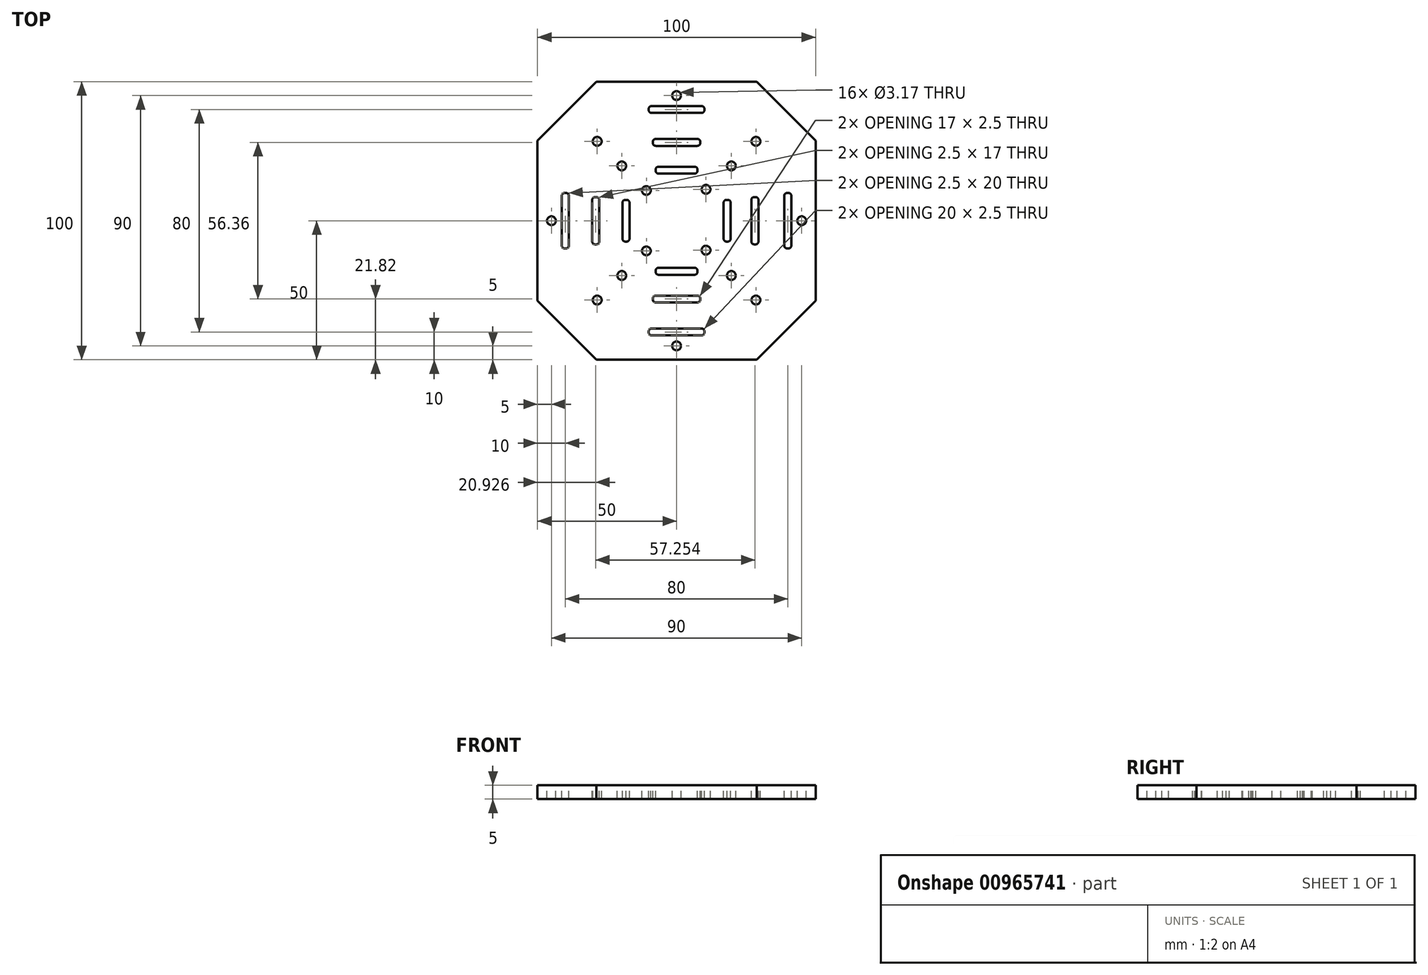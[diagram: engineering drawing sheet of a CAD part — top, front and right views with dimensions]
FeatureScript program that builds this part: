
annotation { "Feature Type Name" : "Feature", "Feature Type Description" : "" }
export const myFeature = defineFeature(function(context is Context, id is Id, definition is map)
    precondition{}
    {
        {
            var Q0;
            Q0=qCreatedBy(makeId("Top.planeOp"),FACE);
            var sketch = newSketch(context, id + "F0", { "sketchPlane" : qUnion([Q0])});
            skLineSegment(sketch, "E0.bottom", {"start": v(50, 50) * mm, "end": v(-50, 50) * mm});
            skLineSegment(sketch, "E0.top", {"start": v(50, -50) * mm, "end": v(-50, -50) * mm});
            skLineSegment(sketch, "E0.left", {"start": v(50, 50) * mm, "end": v(50, -50) * mm});
            skLineSegment(sketch, "E0.right", {"start": v(-50, 50) * mm, "end": v(-50, -50) * mm});
            skPoint(sketch, "E0.middle", {"position": v(0, 0) * mm});
            skSolve(sketch);
        }
        {
            var Q0;
            Q0 = qSketchRegion(id + "F0", true);
            extrude(context, id + "F1", {"entities" : qUnion([Q0]), "depth" : 5 * mm, "offsetDistance" : 25 * mm});
        }
        {
            var Q0;
            Q0=makeQuery(id+"F1.opExtrude","SWEPT_EDGE",EDGE,{"disambiguationData":[OSD([sQuery(id+"F0.wireOp",EDGE,"E0.top"),sQuery(id+"F0.wireOp",EDGE,"E0.left")])]});
            var Q1;
            Q1=makeQuery(id+"F1.opExtrude","SWEPT_EDGE",EDGE,{"disambiguationData":[OSD([sQuery(id+"F0.wireOp",EDGE,"E0.bottom"),sQuery(id+"F0.wireOp",EDGE,"E0.left")])]});
            var Q2;
            Q2=makeQuery(id+"F1.opExtrude","SWEPT_EDGE",EDGE,{"disambiguationData":[OSD([sQuery(id+"F0.wireOp",EDGE,"E0.top"),sQuery(id+"F0.wireOp",EDGE,"E0.right")])]});
            var Q3;
            Q3=makeQuery(id+"F1.opExtrude","SWEPT_EDGE",EDGE,{"disambiguationData":[OSD([sQuery(id+"F0.wireOp",EDGE,"E0.bottom"),sQuery(id+"F0.wireOp",EDGE,"E0.right")])]});
            chamfer(context, id + "F2", {"entities" : qUnion([Q0, Q1, Q2, Q3]), "chamferType" : ChamferType.OFFSET_ANGLE, "width" : 21.21 * mm, "oppositeDirection" : false, "angle" : 45 * degree, "tangentPropagation" : true});
        }
        {
            var Q0;
            Q0=makeQuery(id+"F1.opExtrude","CAP_FACE",FACE,{"disambiguationData":[OSD([sQuery(id+"F0.wireOp",EDGE,"E0.bottom"),sQuery(id+"F0.wireOp",EDGE,"E0.top"),sQuery(id+"F0.wireOp",EDGE,"E0.left"),sQuery(id+"F0.wireOp",EDGE,"E0.right")])],"isStart":false});
            var sketch = newSketch(context, id + "F3", { "sketchPlane" : qUnion([Q0])});
            skPoint(sketch, "E1.middle", {"position": v(0, 40) * mm});
            skLineSegment(sketch, "E2.bottom", {"start": v(41.25, -10) * mm, "end": v(38.75, -10) * mm});
            skLineSegment(sketch, "E2.top", {"start": v(41.25, 10) * mm, "end": v(38.75, 10) * mm});
            skLineSegment(sketch, "E2.left", {"start": v(41.25, -10) * mm, "end": v(41.25, 10) * mm});
            skLineSegment(sketch, "E2.right", {"start": v(38.75, -10) * mm, "end": v(38.75, 10) * mm});
            skPoint(sketch, "E2.middle", {"position": v(40, 0) * mm});
            skLineSegment(sketch, "E3.bottom", {"start": v(-38.75, 10) * mm, "end": v(-41.25, 10) * mm});
            skLineSegment(sketch, "E3.top", {"start": v(-38.75, -10) * mm, "end": v(-41.25, -10) * mm});
            skLineSegment(sketch, "E3.left", {"start": v(-38.75, 10) * mm, "end": v(-38.75, -10) * mm});
            skLineSegment(sketch, "E3.right", {"start": v(-41.25, 10) * mm, "end": v(-41.25, -10) * mm});
            skPoint(sketch, "E3.middle", {"position": v(-40, 0) * mm});
            skLineSegment(sketch, "E4.bottom", {"start": v(10, -41.25) * mm, "end": v(-10, -41.25) * mm});
            skLineSegment(sketch, "E4.top", {"start": v(10, -38.75) * mm, "end": v(-10, -38.75) * mm});
            skLineSegment(sketch, "E4.left", {"start": v(10, -41.25) * mm, "end": v(10, -38.75) * mm});
            skLineSegment(sketch, "E4.right", {"start": v(-10, -41.25) * mm, "end": v(-10, -38.75) * mm});
            skPoint(sketch, "E4.middle", {"position": v(0, -40) * mm});
            skLineSegment(sketch, "E5.bottom", {"start": v(10, 41.25) * mm, "end": v(-10, 41.25) * mm});
            skLineSegment(sketch, "E5.top", {"start": v(10, 38.75) * mm, "end": v(-10, 38.75) * mm});
            skLineSegment(sketch, "E5.left", {"start": v(10, 41.25) * mm, "end": v(10, 38.75) * mm});
            skLineSegment(sketch, "E5.right", {"start": v(-10, 41.25) * mm, "end": v(-10, 38.75) * mm});
            skCircle(sketch, "E6", {"center": v(-45, 0) * mm, "radius": 1.59 * mm});
            skCircle(sketch, "E7", {"center": v(0, 45) * mm, "radius": 1.59 * mm});
            skCircle(sketch, "E8", {"center": v(0, -45) * mm, "radius": 1.59 * mm});
            skCircle(sketch, "E9", {"center": v(45, 0) * mm, "radius": 1.59 * mm});
            skCircle(sketch, "E10", {"center": v(-28.54, 28.54) * mm, "radius": 1.59 * mm});
            skCircle(sketch, "E11", {"center": v(-19.7, 19.7) * mm, "radius": 1.59 * mm});
            skCircle(sketch, "E12", {"center": v(-10.86, 10.86) * mm, "radius": 1.59 * mm});
            skCircle(sketch, "E13", {"center": v(10.6, 11.28) * mm, "radius": 1.59 * mm});
            skCircle(sketch, "E14", {"center": v(19.7, 19.7) * mm, "radius": 1.59 * mm});
            skCircle(sketch, "E15", {"center": v(28.54, 28.54) * mm, "radius": 1.59 * mm});
            skCircle(sketch, "E16", {"center": v(10.6, -10.6) * mm, "radius": 1.59 * mm});
            skCircle(sketch, "E17", {"center": v(19.7, -19.7) * mm, "radius": 1.59 * mm});
            skCircle(sketch, "E18", {"center": v(28.54, -28.54) * mm, "radius": 1.59 * mm});
            skCircle(sketch, "E19", {"center": v(-28.54, -28.54) * mm, "radius": 1.59 * mm});
            skCircle(sketch, "E20", {"center": v(-19.7, -19.7) * mm, "radius": 1.59 * mm});
            skCircle(sketch, "E21", {"center": v(-10.86, -10.86) * mm, "radius": 1.59 * mm});
            skSolve(sketch);
        }
        {
            var Q0;
            Q0=makeQuery(id+"F3.imprint","IMPRINT",FACE,{"disambiguationData":[TD([[makeQuery(id+"F3.imprint","IMPRINT",EDGE,{"derivedFrom":sQuery(id+"F3.wireOp",EDGE,"E2.bottom")}),-1.0]])]});
            var Q1;
            Q1=makeQuery(id+"F3.imprint","IMPRINT",FACE,{"disambiguationData":[TD([[makeQuery(id+"F3.imprint","IMPRINT",EDGE,{"derivedFrom":sQuery(id+"F3.wireOp",EDGE,"E9")}),1.0]])]});
            var Q2;
            Q2=makeQuery(id+"F3.imprint","IMPRINT",FACE,{"disambiguationData":[TD([[makeQuery(id+"F3.imprint","IMPRINT",EDGE,{"derivedFrom":sQuery(id+"F3.wireOp",EDGE,"E7")}),1.0]])]});
            var Q3;
            Q3=makeQuery(id+"F3.imprint","IMPRINT",FACE,{"disambiguationData":[TD([[makeQuery(id+"F3.imprint","IMPRINT",EDGE,{"derivedFrom":sQuery(id+"F3.wireOp",EDGE,"E5.bottom")}),1.0]])]});
            var Q4;
            Q4=makeQuery(id+"F3.imprint","IMPRINT",FACE,{"disambiguationData":[TD([[makeQuery(id+"F3.imprint","IMPRINT",EDGE,{"derivedFrom":sQuery(id+"F3.wireOp",EDGE,"E14")}),1.0]])]});
            var Q5;
            Q5=makeQuery(id+"F3.imprint","IMPRINT",FACE,{"disambiguationData":[TD([[makeQuery(id+"F3.imprint","IMPRINT",EDGE,{"derivedFrom":sQuery(id+"F3.wireOp",EDGE,"E10")}),1.0]])]});
            var Q6;
            Q6=makeQuery(id+"F3.imprint","IMPRINT",FACE,{"disambiguationData":[TD([[makeQuery(id+"F3.imprint","IMPRINT",EDGE,{"derivedFrom":sQuery(id+"F3.wireOp",EDGE,"E15")}),1.0]])]});
            var Q7;
            Q7=makeQuery(id+"F3.imprint","IMPRINT",FACE,{"disambiguationData":[TD([[makeQuery(id+"F3.imprint","IMPRINT",EDGE,{"derivedFrom":sQuery(id+"F3.wireOp",EDGE,"E13")}),1.0]])]});
            var Q8;
            Q8=makeQuery(id+"F3.imprint","IMPRINT",FACE,{"disambiguationData":[TD([[makeQuery(id+"F3.imprint","IMPRINT",EDGE,{"derivedFrom":sQuery(id+"F3.wireOp",EDGE,"E11")}),1.0]])]});
            var Q9;
            Q9=makeQuery(id+"F3.imprint","IMPRINT",FACE,{"disambiguationData":[TD([[makeQuery(id+"F3.imprint","IMPRINT",EDGE,{"derivedFrom":sQuery(id+"F3.wireOp",EDGE,"E6")}),1.0]])]});
            var Q10;
            Q10=makeQuery(id+"F3.imprint","IMPRINT",FACE,{"disambiguationData":[TD([[makeQuery(id+"F3.imprint","IMPRINT",EDGE,{"derivedFrom":sQuery(id+"F3.wireOp",EDGE,"E3.bottom")}),1.0]])]});
            var Q11;
            Q11=makeQuery(id+"F3.imprint","IMPRINT",FACE,{"disambiguationData":[TD([[makeQuery(id+"F3.imprint","IMPRINT",EDGE,{"derivedFrom":sQuery(id+"F3.wireOp",EDGE,"E12")}),1.0]])]});
            var Q12;
            Q12=makeQuery(id+"F3.imprint","IMPRINT",FACE,{"disambiguationData":[TD([[makeQuery(id+"F3.imprint","IMPRINT",EDGE,{"derivedFrom":sQuery(id+"F3.wireOp",EDGE,"E8")}),1.0]])]});
            var Q13;
            Q13=makeQuery(id+"F3.imprint","IMPRINT",FACE,{"disambiguationData":[TD([[makeQuery(id+"F3.imprint","IMPRINT",EDGE,{"derivedFrom":sQuery(id+"F3.wireOp",EDGE,"E4.bottom")}),-1.0]])]});
            var Q14;
            Q14=makeQuery(id+"F3.imprint","IMPRINT",FACE,{"disambiguationData":[TD([[makeQuery(id+"F3.imprint","IMPRINT",EDGE,{"derivedFrom":sQuery(id+"F3.wireOp",EDGE,"E16")}),1.0]])]});
            var Q15;
            Q15=makeQuery(id+"F3.imprint","IMPRINT",FACE,{"disambiguationData":[TD([[makeQuery(id+"F3.imprint","IMPRINT",EDGE,{"derivedFrom":sQuery(id+"F3.wireOp",EDGE,"E17")}),1.0]])]});
            var Q16;
            Q16=makeQuery(id+"F3.imprint","IMPRINT",FACE,{"disambiguationData":[TD([[makeQuery(id+"F3.imprint","IMPRINT",EDGE,{"derivedFrom":sQuery(id+"F3.wireOp",EDGE,"E18")}),1.0]])]});
            var Q17;
            Q17=makeQuery(id+"F3.imprint","IMPRINT",FACE,{"disambiguationData":[TD([[makeQuery(id+"F3.imprint","IMPRINT",EDGE,{"derivedFrom":sQuery(id+"F3.wireOp",EDGE,"E19")}),1.0]])]});
            var Q18;
            Q18=makeQuery(id+"F3.imprint","IMPRINT",FACE,{"disambiguationData":[TD([[makeQuery(id+"F3.imprint","IMPRINT",EDGE,{"derivedFrom":sQuery(id+"F3.wireOp",EDGE,"E20")}),1.0]])]});
            var Q19;
            Q19=makeQuery(id+"F3.imprint","IMPRINT",FACE,{"disambiguationData":[TD([[makeQuery(id+"F3.imprint","IMPRINT",EDGE,{"derivedFrom":sQuery(id+"F3.wireOp",EDGE,"E21")}),1.0]])]});
            extrude(context, id + "F4", {"entities" : qUnion([Q0, Q1, Q2, Q3, Q4, Q5, Q6, Q7, Q8, Q9, Q10, Q11, Q12, Q13, Q14, Q15, Q16, Q17, Q18, Q19]), "operationType" : NewBodyOperationType.REMOVE, "oppositeDirection" : true, "depth" : 5 * mm, "offsetDistance" : 25 * mm});
        }
        {
            var Q0;
            Q0=makeQuery(id+"F4.boolean.opBoolean","COPY",EDGE,{"derivedFrom":makeQuery(id+"F4.opExtrude","SWEPT_EDGE",EDGE,{"disambiguationData":[OSD([sQuery(id+"F3.wireOp",EDGE,"E3.bottom"),sQuery(id+"F3.wireOp",EDGE,"E3.right")])]})});
            var Q1;
            Q1=makeQuery(id+"F4.boolean.opBoolean","COPY",EDGE,{"derivedFrom":makeQuery(id+"F4.opExtrude","SWEPT_EDGE",EDGE,{"disambiguationData":[OSD([sQuery(id+"F3.wireOp",EDGE,"E4.top"),sQuery(id+"F3.wireOp",EDGE,"E4.right")])]})});
            var Q2;
            Q2=makeQuery(id+"F4.boolean.opBoolean","COPY",EDGE,{"derivedFrom":makeQuery(id+"F4.opExtrude","SWEPT_EDGE",EDGE,{"disambiguationData":[OSD([sQuery(id+"F3.wireOp",EDGE,"E2.top"),sQuery(id+"F3.wireOp",EDGE,"E2.right")])]})});
            var Q3;
            Q3=makeQuery(id+"F4.boolean.opBoolean","COPY",EDGE,{"derivedFrom":makeQuery(id+"F4.opExtrude","SWEPT_EDGE",EDGE,{"disambiguationData":[OSD([sQuery(id+"F3.wireOp",EDGE,"E5.bottom"),sQuery(id+"F3.wireOp",EDGE,"E5.right")])]})});
            var Q4;
            Q4=makeQuery(id+"F4.boolean.opBoolean","COPY",EDGE,{"derivedFrom":makeQuery(id+"F4.opExtrude","SWEPT_EDGE",EDGE,{"disambiguationData":[OSD([sQuery(id+"F3.wireOp",EDGE,"E4.top"),sQuery(id+"F3.wireOp",EDGE,"E4.left")])]})});
            var Q5;
            Q5=makeQuery(id+"F4.boolean.opBoolean","COPY",EDGE,{"derivedFrom":makeQuery(id+"F4.opExtrude","SWEPT_EDGE",EDGE,{"disambiguationData":[OSD([sQuery(id+"F3.wireOp",EDGE,"E2.top"),sQuery(id+"F3.wireOp",EDGE,"E2.left")])]})});
            var Q6;
            Q6=makeQuery(id+"F4.boolean.opBoolean","COPY",EDGE,{"derivedFrom":makeQuery(id+"F4.opExtrude","SWEPT_EDGE",EDGE,{"disambiguationData":[OSD([sQuery(id+"F3.wireOp",EDGE,"E3.bottom"),sQuery(id+"F3.wireOp",EDGE,"E3.left")])]})});
            var Q7;
            Q7=makeQuery(id+"F4.boolean.opBoolean","COPY",EDGE,{"derivedFrom":makeQuery(id+"F4.opExtrude","SWEPT_EDGE",EDGE,{"disambiguationData":[OSD([sQuery(id+"F3.wireOp",EDGE,"E5.bottom"),sQuery(id+"F3.wireOp",EDGE,"E5.left")])]})});
            var Q8;
            Q8=makeQuery(id+"F4.boolean.opBoolean","COPY",EDGE,{"derivedFrom":makeQuery(id+"F4.opExtrude","SWEPT_EDGE",EDGE,{"disambiguationData":[OSD([sQuery(id+"F3.wireOp",EDGE,"E2.bottom"),sQuery(id+"F3.wireOp",EDGE,"E2.left")])]})});
            var Q9;
            Q9=makeQuery(id+"F4.boolean.opBoolean","COPY",EDGE,{"derivedFrom":makeQuery(id+"F4.opExtrude","SWEPT_EDGE",EDGE,{"disambiguationData":[OSD([sQuery(id+"F3.wireOp",EDGE,"E4.bottom"),sQuery(id+"F3.wireOp",EDGE,"E4.left")])]})});
            var Q10;
            Q10=makeQuery(id+"F4.boolean.opBoolean","COPY",EDGE,{"derivedFrom":makeQuery(id+"F4.opExtrude","SWEPT_EDGE",EDGE,{"disambiguationData":[OSD([sQuery(id+"F3.wireOp",EDGE,"E5.top"),sQuery(id+"F3.wireOp",EDGE,"E5.left")])]})});
            var Q11;
            Q11=makeQuery(id+"F4.boolean.opBoolean","COPY",EDGE,{"derivedFrom":makeQuery(id+"F4.opExtrude","SWEPT_EDGE",EDGE,{"disambiguationData":[OSD([sQuery(id+"F3.wireOp",EDGE,"E3.top"),sQuery(id+"F3.wireOp",EDGE,"E3.left")])]})});
            var Q12;
            Q12=makeQuery(id+"F4.boolean.opBoolean","COPY",EDGE,{"derivedFrom":makeQuery(id+"F4.opExtrude","SWEPT_EDGE",EDGE,{"disambiguationData":[OSD([sQuery(id+"F3.wireOp",EDGE,"E5.top"),sQuery(id+"F3.wireOp",EDGE,"E5.right")])]})});
            var Q13;
            Q13=makeQuery(id+"F4.boolean.opBoolean","COPY",EDGE,{"derivedFrom":makeQuery(id+"F4.opExtrude","SWEPT_EDGE",EDGE,{"disambiguationData":[OSD([sQuery(id+"F3.wireOp",EDGE,"E2.bottom"),sQuery(id+"F3.wireOp",EDGE,"E2.right")])]})});
            var Q14;
            Q14=makeQuery(id+"F4.boolean.opBoolean","COPY",EDGE,{"derivedFrom":makeQuery(id+"F4.opExtrude","SWEPT_EDGE",EDGE,{"disambiguationData":[OSD([sQuery(id+"F3.wireOp",EDGE,"E3.top"),sQuery(id+"F3.wireOp",EDGE,"E3.right")])]})});
            var Q15;
            Q15=makeQuery(id+"F4.boolean.opBoolean","COPY",EDGE,{"derivedFrom":makeQuery(id+"F4.opExtrude","SWEPT_EDGE",EDGE,{"disambiguationData":[OSD([sQuery(id+"F3.wireOp",EDGE,"E4.bottom"),sQuery(id+"F3.wireOp",EDGE,"E4.right")])]})});
            fillet(context, id + "F5", {"entities" : qUnion([Q0, Q1, Q2, Q3, Q4, Q5, Q6, Q7, Q8, Q9, Q10, Q11, Q12, Q13, Q14, Q15]), "radius" : 1 * mm, "tangentPropagation" : true, "allowEdgeOverflow" : false});
        }
        {
            var Q0;
            Q0=makeQuery(id+"F1.opExtrude","CAP_FACE",FACE,{"disambiguationData":[OSD([sQuery(id+"F0.wireOp",EDGE,"E0.bottom"),sQuery(id+"F0.wireOp",EDGE,"E0.top"),sQuery(id+"F0.wireOp",EDGE,"E0.left"),sQuery(id+"F0.wireOp",EDGE,"E0.right")])],"isStart":false});
            var sketch = newSketch(context, id + "F6", { "sketchPlane" : qUnion([Q0])});
            skLineSegment(sketch, "E22", {"start": v(-18.18, 18.18) * mm, "end": v(-7.5, 18.18) * mm});
            skLineSegment(sketch, "E23.bottom", {"start": v(7.5, 19.43) * mm, "end": v(-7.5, 19.43) * mm});
            skLineSegment(sketch, "E23.top", {"start": v(7.5, 16.93) * mm, "end": v(-7.5, 16.93) * mm});
            skLineSegment(sketch, "E23.left", {"start": v(7.5, 19.43) * mm, "end": v(7.5, 16.93) * mm});
            skLineSegment(sketch, "E23.right", {"start": v(-7.5, 19.43) * mm, "end": v(-7.5, 16.93) * mm});
            skPoint(sketch, "E23.middle", {"position": v(0, 18.18) * mm});
            skLineSegment(sketch, "E24.bottom", {"start": v(-19.43, 7.5) * mm, "end": v(-16.93, 7.5) * mm});
            skLineSegment(sketch, "E24.top", {"start": v(-19.43, -7.5) * mm, "end": v(-16.93, -7.5) * mm});
            skLineSegment(sketch, "E24.left", {"start": v(-19.43, 7.5) * mm, "end": v(-19.43, -7.5) * mm});
            skLineSegment(sketch, "E24.right", {"start": v(-16.93, 7.5) * mm, "end": v(-16.93, -7.5) * mm});
            skPoint(sketch, "E24.middle", {"position": v(-18.18, 0) * mm});
            skLineSegment(sketch, "E25.bottom", {"start": v(7.5, -16.93) * mm, "end": v(-7.5, -16.93) * mm});
            skLineSegment(sketch, "E25.top", {"start": v(7.5, -19.43) * mm, "end": v(-7.5, -19.43) * mm});
            skLineSegment(sketch, "E25.left", {"start": v(7.5, -16.93) * mm, "end": v(7.5, -19.43) * mm});
            skLineSegment(sketch, "E25.right", {"start": v(-7.5, -16.93) * mm, "end": v(-7.5, -19.43) * mm});
            skPoint(sketch, "E25.middle", {"position": v(0, -18.18) * mm});
            skLineSegment(sketch, "E26.bottom", {"start": v(19.43, 7.5) * mm, "end": v(16.93, 7.5) * mm});
            skLineSegment(sketch, "E26.top", {"start": v(19.43, -7.5) * mm, "end": v(16.93, -7.5) * mm});
            skLineSegment(sketch, "E26.left", {"start": v(19.43, 7.5) * mm, "end": v(19.43, -7.5) * mm});
            skLineSegment(sketch, "E26.right", {"start": v(16.93, 7.5) * mm, "end": v(16.93, -7.5) * mm});
            skPoint(sketch, "E26.middle", {"position": v(18.18, 0) * mm});
            skLineSegment(sketch, "E27.bottom", {"start": v(-27.82, 8.5) * mm, "end": v(-30.32, 8.5) * mm});
            skLineSegment(sketch, "E27.top", {"start": v(-27.82, -8.5) * mm, "end": v(-30.32, -8.5) * mm});
            skLineSegment(sketch, "E27.left", {"start": v(-27.82, 8.5) * mm, "end": v(-27.82, -8.5) * mm});
            skLineSegment(sketch, "E27.right", {"start": v(-30.32, 8.5) * mm, "end": v(-30.32, -8.5) * mm});
            skPoint(sketch, "E27.middle", {"position": v(-29.07, 0) * mm});
            skLineSegment(sketch, "E28", {"start": v(0, 18.18) * mm, "end": v(0, 19.43) * mm});
            skLineSegment(sketch, "E29", {"start": v(0, -18.18) * mm, "end": v(0, -19.43) * mm});
            skLineSegment(sketch, "E30.bottom", {"start": v(8.5, -26.93) * mm, "end": v(-8.5, -26.93) * mm});
            skLineSegment(sketch, "E30.top", {"start": v(8.5, -29.43) * mm, "end": v(-8.5, -29.43) * mm});
            skLineSegment(sketch, "E30.left", {"start": v(8.5, -26.93) * mm, "end": v(8.5, -29.43) * mm});
            skLineSegment(sketch, "E30.right", {"start": v(-8.5, -26.93) * mm, "end": v(-8.5, -29.43) * mm});
            skPoint(sketch, "E30.middle", {"position": v(0, -28.18) * mm});
            skLineSegment(sketch, "E31.bottom", {"start": v(29.43, 8.5) * mm, "end": v(26.93, 8.5) * mm});
            skLineSegment(sketch, "E31.top", {"start": v(29.43, -8.5) * mm, "end": v(26.93, -8.5) * mm});
            skLineSegment(sketch, "E31.left", {"start": v(29.43, 8.5) * mm, "end": v(29.43, -8.5) * mm});
            skLineSegment(sketch, "E31.right", {"start": v(26.93, 8.5) * mm, "end": v(26.93, -8.5) * mm});
            skPoint(sketch, "E31.middle", {"position": v(28.18, 0) * mm});
            skLineSegment(sketch, "E32.bottom", {"start": v(8.5, 29.43) * mm, "end": v(-8.5, 29.43) * mm});
            skLineSegment(sketch, "E32.top", {"start": v(8.5, 26.93) * mm, "end": v(-8.5, 26.93) * mm});
            skLineSegment(sketch, "E32.left", {"start": v(8.5, 29.43) * mm, "end": v(8.5, 26.93) * mm});
            skLineSegment(sketch, "E32.right", {"start": v(-8.5, 29.43) * mm, "end": v(-8.5, 26.93) * mm});
            skPoint(sketch, "E32.middle", {"position": v(0, 28.18) * mm});
            skLineSegment(sketch, "E33.trimOffspring", {"start": v(-27.82, 0) * mm, "end": v(-29.07, 0) * mm});
            skPoint(sketch, "E34.orphan", {"position": v(-18.18, -18.18) * mm});
            skLineSegment(sketch, "E35.trimOffspring", {"start": v(0, -26.93) * mm, "end": v(0, -28.18) * mm});
            skLineSegment(sketch, "E36.trimOffspring", {"start": v(0, 26.93) * mm, "end": v(0, 28.18) * mm});
            skPoint(sketch, "E37.orphan", {"position": v(18.18, 18.18) * mm});
            skLineSegment(sketch, "E38.trimOffspring", {"start": v(26.93, 0) * mm, "end": v(28.18, 0) * mm});
            skPoint(sketch, "E39.end.orphan", {"position": v(18.18, -18.18) * mm});
            skSolve(sketch);
        }
        {
            var Q0;
            Q0 = qSketchRegion(id + "F6", true);
            extrude(context, id + "F7", {"entities" : qUnion([Q0]), "operationType" : NewBodyOperationType.REMOVE, "oppositeDirection" : true, "depth" : 5 * mm, "offsetDistance" : 25 * mm});
        }
        {
            var Q0;
            Q0=makeQuery(id+"F7.boolean.opBoolean","COPY",EDGE,{"derivedFrom":makeQuery(id+"F7.opExtrude","SWEPT_EDGE",EDGE,{"disambiguationData":[OSD([sQuery(id+"F6.wireOp",EDGE,"E27.bottom"),sQuery(id+"F6.wireOp",EDGE,"E27.right")])]})});
            var Q1;
            Q1=makeQuery(id+"F7.boolean.opBoolean","COPY",EDGE,{"derivedFrom":makeQuery(id+"F7.opExtrude","SWEPT_EDGE",EDGE,{"disambiguationData":[OSD([sQuery(id+"F6.wireOp",EDGE,"E24.bottom"),sQuery(id+"F6.wireOp",EDGE,"E24.left")])]})});
            var Q2;
            Q2=makeQuery(id+"F7.boolean.opBoolean","COPY",EDGE,{"derivedFrom":makeQuery(id+"F7.opExtrude","SWEPT_EDGE",EDGE,{"disambiguationData":[OSD([sQuery(id+"F6.wireOp",EDGE,"E32.bottom"),sQuery(id+"F6.wireOp",EDGE,"E32.right")])]})});
            var Q3;
            Q3=makeQuery(id+"F7.boolean.opBoolean","COPY",EDGE,{"derivedFrom":makeQuery(id+"F7.opExtrude","SWEPT_EDGE",EDGE,{"disambiguationData":[OSD([sQuery(id+"F6.wireOp",EDGE,"E23.bottom"),sQuery(id+"F6.wireOp",EDGE,"E23.right")])]})});
            var Q4;
            Q4=makeQuery(id+"F7.boolean.opBoolean","COPY",EDGE,{"derivedFrom":makeQuery(id+"F7.opExtrude","SWEPT_EDGE",EDGE,{"disambiguationData":[OSD([sQuery(id+"F6.wireOp",EDGE,"E25.bottom"),sQuery(id+"F6.wireOp",EDGE,"E25.right")])]})});
            var Q5;
            Q5=makeQuery(id+"F7.boolean.opBoolean","COPY",EDGE,{"derivedFrom":makeQuery(id+"F7.opExtrude","SWEPT_EDGE",EDGE,{"disambiguationData":[OSD([sQuery(id+"F6.wireOp",EDGE,"E30.bottom"),sQuery(id+"F6.wireOp",EDGE,"E30.right")])]})});
            var Q6;
            Q6=makeQuery(id+"F7.boolean.opBoolean","COPY",EDGE,{"derivedFrom":makeQuery(id+"F7.opExtrude","SWEPT_EDGE",EDGE,{"disambiguationData":[OSD([sQuery(id+"F6.wireOp",EDGE,"E26.bottom"),sQuery(id+"F6.wireOp",EDGE,"E26.right")])]})});
            var Q7;
            Q7=makeQuery(id+"F7.boolean.opBoolean","COPY",EDGE,{"derivedFrom":makeQuery(id+"F7.opExtrude","SWEPT_EDGE",EDGE,{"disambiguationData":[OSD([sQuery(id+"F6.wireOp",EDGE,"E31.bottom"),sQuery(id+"F6.wireOp",EDGE,"E31.right")])]})});
            var Q8;
            Q8=makeQuery(id+"F7.boolean.opBoolean","COPY",EDGE,{"derivedFrom":makeQuery(id+"F7.opExtrude","SWEPT_EDGE",EDGE,{"disambiguationData":[OSD([sQuery(id+"F6.wireOp",EDGE,"E32.bottom"),sQuery(id+"F6.wireOp",EDGE,"E32.left")])]})});
            var Q9;
            Q9=makeQuery(id+"F7.boolean.opBoolean","COPY",EDGE,{"derivedFrom":makeQuery(id+"F7.opExtrude","SWEPT_EDGE",EDGE,{"disambiguationData":[OSD([sQuery(id+"F6.wireOp",EDGE,"E23.bottom"),sQuery(id+"F6.wireOp",EDGE,"E23.left")])]})});
            var Q10;
            Q10=makeQuery(id+"F7.boolean.opBoolean","COPY",EDGE,{"derivedFrom":makeQuery(id+"F7.opExtrude","SWEPT_EDGE",EDGE,{"disambiguationData":[OSD([sQuery(id+"F6.wireOp",EDGE,"E27.bottom"),sQuery(id+"F6.wireOp",EDGE,"E27.left")])]})});
            var Q11;
            Q11=makeQuery(id+"F7.boolean.opBoolean","COPY",EDGE,{"derivedFrom":makeQuery(id+"F7.opExtrude","SWEPT_EDGE",EDGE,{"disambiguationData":[OSD([sQuery(id+"F6.wireOp",EDGE,"E24.bottom"),sQuery(id+"F6.wireOp",EDGE,"E24.right")])]})});
            var Q12;
            Q12=makeQuery(id+"F7.boolean.opBoolean","COPY",EDGE,{"derivedFrom":makeQuery(id+"F7.opExtrude","SWEPT_EDGE",EDGE,{"disambiguationData":[OSD([sQuery(id+"F6.wireOp",EDGE,"E31.bottom"),sQuery(id+"F6.wireOp",EDGE,"E31.left")])]})});
            var Q13;
            Q13=makeQuery(id+"F7.boolean.opBoolean","COPY",EDGE,{"derivedFrom":makeQuery(id+"F7.opExtrude","SWEPT_EDGE",EDGE,{"disambiguationData":[OSD([sQuery(id+"F6.wireOp",EDGE,"E26.bottom"),sQuery(id+"F6.wireOp",EDGE,"E26.left")])]})});
            var Q14;
            Q14=makeQuery(id+"F7.boolean.opBoolean","COPY",EDGE,{"derivedFrom":makeQuery(id+"F7.opExtrude","SWEPT_EDGE",EDGE,{"disambiguationData":[OSD([sQuery(id+"F6.wireOp",EDGE,"E25.bottom"),sQuery(id+"F6.wireOp",EDGE,"E25.left")])]})});
            var Q15;
            Q15=makeQuery(id+"F7.boolean.opBoolean","COPY",EDGE,{"derivedFrom":makeQuery(id+"F7.opExtrude","SWEPT_EDGE",EDGE,{"disambiguationData":[OSD([sQuery(id+"F6.wireOp",EDGE,"E30.bottom"),sQuery(id+"F6.wireOp",EDGE,"E30.left")])]})});
            var Q16;
            Q16=makeQuery(id+"F7.boolean.opBoolean","COPY",EDGE,{"derivedFrom":makeQuery(id+"F7.opExtrude","SWEPT_EDGE",EDGE,{"disambiguationData":[OSD([sQuery(id+"F6.wireOp",EDGE,"E31.top"),sQuery(id+"F6.wireOp",EDGE,"E31.left")])]})});
            var Q17;
            Q17=makeQuery(id+"F7.boolean.opBoolean","COPY",EDGE,{"derivedFrom":makeQuery(id+"F7.opExtrude","SWEPT_EDGE",EDGE,{"disambiguationData":[OSD([sQuery(id+"F6.wireOp",EDGE,"E26.top"),sQuery(id+"F6.wireOp",EDGE,"E26.left")])]})});
            var Q18;
            Q18=makeQuery(id+"F7.boolean.opBoolean","COPY",EDGE,{"derivedFrom":makeQuery(id+"F7.opExtrude","SWEPT_EDGE",EDGE,{"disambiguationData":[OSD([sQuery(id+"F6.wireOp",EDGE,"E25.top"),sQuery(id+"F6.wireOp",EDGE,"E25.left")])]})});
            var Q19;
            Q19=makeQuery(id+"F7.boolean.opBoolean","COPY",EDGE,{"derivedFrom":makeQuery(id+"F7.opExtrude","SWEPT_EDGE",EDGE,{"disambiguationData":[OSD([sQuery(id+"F6.wireOp",EDGE,"E30.top"),sQuery(id+"F6.wireOp",EDGE,"E30.left")])]})});
            var Q20;
            Q20=makeQuery(id+"F7.boolean.opBoolean","COPY",EDGE,{"derivedFrom":makeQuery(id+"F7.opExtrude","SWEPT_EDGE",EDGE,{"disambiguationData":[OSD([sQuery(id+"F6.wireOp",EDGE,"E23.top"),sQuery(id+"F6.wireOp",EDGE,"E23.left")])]})});
            var Q21;
            Q21=makeQuery(id+"F7.boolean.opBoolean","COPY",EDGE,{"derivedFrom":makeQuery(id+"F7.opExtrude","SWEPT_EDGE",EDGE,{"disambiguationData":[OSD([sQuery(id+"F6.wireOp",EDGE,"E32.top"),sQuery(id+"F6.wireOp",EDGE,"E32.left")])]})});
            var Q22;
            Q22=makeQuery(id+"F7.boolean.opBoolean","COPY",EDGE,{"derivedFrom":makeQuery(id+"F7.opExtrude","SWEPT_EDGE",EDGE,{"disambiguationData":[OSD([sQuery(id+"F6.wireOp",EDGE,"E27.top"),sQuery(id+"F6.wireOp",EDGE,"E27.left")])]})});
            var Q23;
            Q23=makeQuery(id+"F7.boolean.opBoolean","COPY",EDGE,{"derivedFrom":makeQuery(id+"F7.opExtrude","SWEPT_EDGE",EDGE,{"disambiguationData":[OSD([sQuery(id+"F6.wireOp",EDGE,"E24.top"),sQuery(id+"F6.wireOp",EDGE,"E24.right")])]})});
            var Q24;
            Q24=makeQuery(id+"F7.boolean.opBoolean","COPY",EDGE,{"derivedFrom":makeQuery(id+"F7.opExtrude","SWEPT_EDGE",EDGE,{"disambiguationData":[OSD([sQuery(id+"F6.wireOp",EDGE,"E25.top"),sQuery(id+"F6.wireOp",EDGE,"E25.right")])]})});
            var Q25;
            Q25=makeQuery(id+"F7.boolean.opBoolean","COPY",EDGE,{"derivedFrom":makeQuery(id+"F7.opExtrude","SWEPT_EDGE",EDGE,{"disambiguationData":[OSD([sQuery(id+"F6.wireOp",EDGE,"E30.top"),sQuery(id+"F6.wireOp",EDGE,"E30.right")])]})});
            var Q26;
            Q26=makeQuery(id+"F7.boolean.opBoolean","COPY",EDGE,{"derivedFrom":makeQuery(id+"F7.opExtrude","SWEPT_EDGE",EDGE,{"disambiguationData":[OSD([sQuery(id+"F6.wireOp",EDGE,"E27.top"),sQuery(id+"F6.wireOp",EDGE,"E27.right")])]})});
            var Q27;
            Q27=makeQuery(id+"F7.boolean.opBoolean","COPY",EDGE,{"derivedFrom":makeQuery(id+"F7.opExtrude","SWEPT_EDGE",EDGE,{"disambiguationData":[OSD([sQuery(id+"F6.wireOp",EDGE,"E24.top"),sQuery(id+"F6.wireOp",EDGE,"E24.left")])]})});
            var Q28;
            Q28=makeQuery(id+"F7.boolean.opBoolean","COPY",EDGE,{"derivedFrom":makeQuery(id+"F7.opExtrude","SWEPT_EDGE",EDGE,{"disambiguationData":[OSD([sQuery(id+"F6.wireOp",EDGE,"E26.top"),sQuery(id+"F6.wireOp",EDGE,"E26.right")])]})});
            var Q29;
            Q29=makeQuery(id+"F7.boolean.opBoolean","COPY",EDGE,{"derivedFrom":makeQuery(id+"F7.opExtrude","SWEPT_EDGE",EDGE,{"disambiguationData":[OSD([sQuery(id+"F6.wireOp",EDGE,"E31.top"),sQuery(id+"F6.wireOp",EDGE,"E31.right")])]})});
            var Q30;
            Q30=makeQuery(id+"F7.boolean.opBoolean","COPY",EDGE,{"derivedFrom":makeQuery(id+"F7.opExtrude","SWEPT_EDGE",EDGE,{"disambiguationData":[OSD([sQuery(id+"F6.wireOp",EDGE,"E32.top"),sQuery(id+"F6.wireOp",EDGE,"E32.right")])]})});
            var Q31;
            Q31=makeQuery(id+"F7.boolean.opBoolean","COPY",EDGE,{"derivedFrom":makeQuery(id+"F7.opExtrude","SWEPT_EDGE",EDGE,{"disambiguationData":[OSD([sQuery(id+"F6.wireOp",EDGE,"E23.top"),sQuery(id+"F6.wireOp",EDGE,"E23.right")])]})});
            fillet(context, id + "F8", {"entities" : qUnion([Q0, Q1, Q2, Q3, Q4, Q5, Q6, Q7, Q8, Q9, Q10, Q11, Q12, Q13, Q14, Q15, Q16, Q17, Q18, Q19, Q20, Q21, Q22, Q23, Q24, Q25, Q26, Q27, Q28, Q29, Q30, Q31]), "radius" : 1 * mm, "tangentPropagation" : true, "allowEdgeOverflow" : false});
        }
    });
